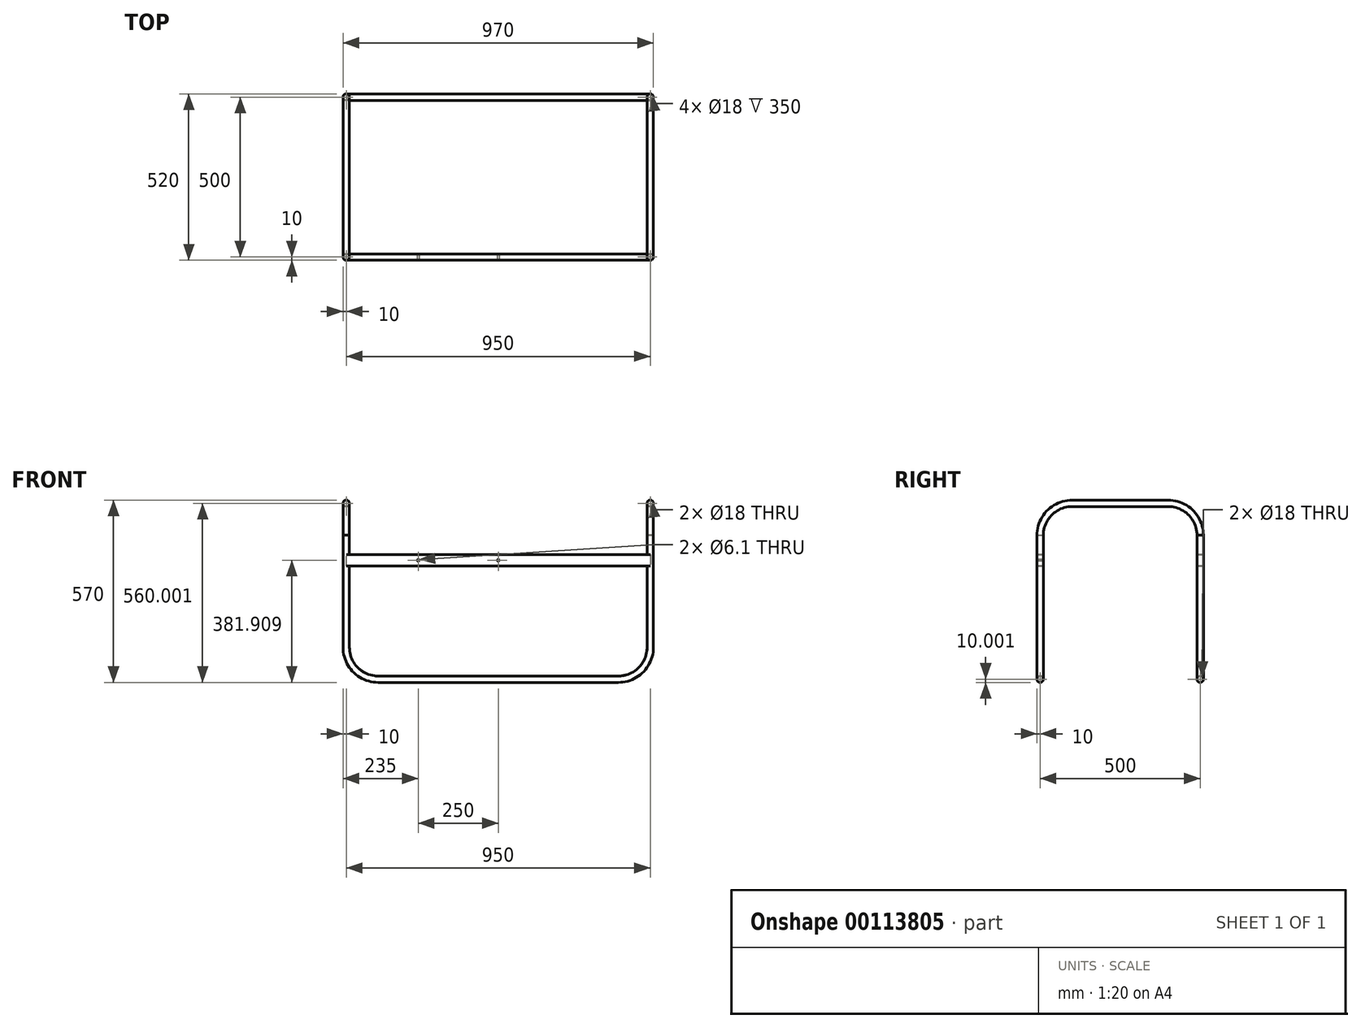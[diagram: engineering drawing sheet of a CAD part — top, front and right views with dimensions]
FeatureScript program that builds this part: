
annotation { "Feature Type Name" : "Feature", "Feature Type Description" : "" }
export const myFeature = defineFeature(function(context is Context, id is Id, definition is map)
    precondition{}
    {
        {
            var Q0;
            Q0=qCreatedBy(makeId("Front.planeOp"),FACE);
            var sketch = newSketch(context, id + "F0", { "sketchPlane" : qUnion([Q0])});
            skLineSegment(sketch, "E0.top", {"start": v(600, -233.58) * mm, "end": v(-150, -233.58) * mm});
            skPoint(sketch, "E1.visualSharp", {"position": v(-150, -233.58) * mm});
            skArc(sketch, "E1.filletArc", {"start": v(-250, -133.58) * mm, "mid": v(-220.71, -204.29) * mm, "end": v(-150, -233.58) * mm});
            skPoint(sketch, "E2.visualSharp", {"position": v(600, -233.58) * mm});
            skArc(sketch, "E2.filletArc", {"start": v(600, -233.58) * mm, "mid": v(670.71, -204.29) * mm, "end": v(700, -133.58) * mm});
            skLineSegment(sketch, "E3", {"start": v(-250, -133.58) * mm, "end": v(-250, 216.42) * mm});
            skLineSegment(sketch, "E4", {"start": v(700, -133.58) * mm, "end": v(700, 216.42) * mm});
            skLineSegment(sketch, "E5", {"start": v(-250, 156.03) * mm, "end": v(700, 156.03) * mm});
            skLineSegment(sketch, "E6", {"start": v(-250, 120.63) * mm, "end": v(700, 120.63) * mm});
            skSolve(sketch);
        }
        {
            var Q0;
            Q0=sQuery(id+"F0.wireOp",VERTEX,"E4.start");
            var Q1;
            Q1=sQuery(id+"F0.wireOp",EDGE,"E0.top");
            cPlane(context, id + "F1", {"entities" : qUnion([Q0, Q1]), "cplaneType" : CPlaneType.LINE_POINT, "offset" : 350 * mm, "width" : 150 * mm, "height" : 150 * mm});
        }
        {
            var Q0;
            Q0=qCreatedBy(id+"F1.planeOp",FACE);
            var sketch = newSketch(context, id + "F2", { "sketchPlane" : qUnion([Q0])});
            skPoint(sketch, "E7.0", {"position": v(0, -175) * mm});
            skLineSegment(sketch, "E8", {"start": v(-100, 316.42) * mm, "end": v(-194.41, 316.42) * mm});
            skPoint(sketch, "E9.0", {"position": v(-500, 216.42) * mm});
            skArc(sketch, "E10", {"start": v(-400, 316.42) * mm, "mid": v(-470.71, 287.13) * mm, "end": v(-500, 216.42) * mm});
            skPoint(sketch, "E11.0", {"position": v(0, 216.42) * mm});
            skArc(sketch, "E12", {"start": v(-100, 316.42) * mm, "mid": v(-77.01, 313.74) * mm, "end": v(-55.26, 305.85) * mm});
            skArc(sketch, "E13", {"start": v(-55.26, 305.85) * mm, "mid": v(-14.93, 268.98) * mm, "end": v(0, 216.42) * mm});
            skPoint(sketch, "E14", {"position": v(-194.77, 316.42) * mm});
            skLineSegment(sketch, "E15", {"start": v(-194.41, 316.42) * mm, "end": v(-400, 316.42) * mm});
            skSolve(sketch);
        }
        {
            var Q0;
            Q0=sQuery(id+"F2.wireOp",EDGE,"E10");
            var Q1;
            Q1=sQuery(id+"F2.wireOp",VERTEX,"E9.0");
            cPlane(context, id + "F3", {"entities" : qUnion([Q0, Q1]), "cplaneType" : CPlaneType.CURVE_POINT, "offset" : 700 * mm, "oppositeDirection" : true, "width" : 150 * mm, "height" : 150 * mm});
        }
        {
            var Q0;
            Q0=qCreatedBy(id+"F3.planeOp",FACE);
            var sketch = newSketch(context, id + "F4", { "sketchPlane" : qUnion([Q0])});
            skPoint(sketch, "E16.0", {"position": v(700, 0) * mm});
            skPoint(sketch, "E17.0", {"position": v(700, -500) * mm});
            skCircle(sketch, "E18", {"center": v(700, -500) * mm, "radius": 10 * mm});
            skCircle(sketch, "E19", {"center": v(700, -500) * mm, "radius": 9 * mm});
            skSolve(sketch);
        }
        {
            var Q0;
            Q0=makeQuery(id+"F4.imprint","IMPRINT",FACE,{"disambiguationData":[TD([[makeQuery(id+"F4.imprint","IMPRINT",EDGE,{"derivedFrom":sQuery(id+"F4.wireOp",EDGE,"E18")}),1.0]])]});
            var Q1;
            Q1=sQuery(id+"F2.wireOp",EDGE,"E10");
            var Q2;
            Q2=sQuery(id+"F2.wireOp",EDGE,"E15");
            var Q3;
            Q3=sQuery(id+"F2.wireOp",EDGE,"E8");
            var Q4;
            Q4=sQuery(id+"F2.wireOp",EDGE,"E12");
            var Q5;
            Q5=sQuery(id+"F2.wireOp",EDGE,"E13");
            var Q6;
            Q6=sQuery(id+"F0.wireOp",EDGE,"E4");
            var Q7;
            Q7=sQuery(id+"F0.wireOp",EDGE,"E2.filletArc");
            var Q8;
            Q8=sQuery(id+"F0.wireOp",EDGE,"E0.top");
            var Q9;
            Q9=sQuery(id+"F0.wireOp",EDGE,"E1.filletArc");
            var Q10;
            Q10=sQuery(id+"F0.wireOp",EDGE,"E3");
            sweep(context, id + "F5", {"profiles" : qUnion([Q0]), "path" : qUnion([Q1, Q2, Q3, Q4, Q5, Q6, Q7, Q8, Q9, Q10])});
        }
        {
            var Q0;
            {var subQ0=sQuery(id+"F0.wireOp",EDGE,"E5");Q0=makeQuery(id+"F0.imprint","IMPRINT",FACE,{"disambiguationData":[TD([[makeQuery(id+"F0.imprint","IMPRINT",EDGE,{"derivedFrom":subQ0}),-1.0]])]});}
            extrude(context, id + "F6", {"entities" : qUnion([Q0]), "operationType" : NewBodyOperationType.ADD, "endBound" : BoundingType.SYMMETRIC, "depth" : 20 * mm});
        }
        {
            var Q0;
            Q0=sQuery(id+"F2.wireOp",VERTEX,"E11.0");
            var Q1;
            Q1=sQuery(id+"F0.wireOp",VERTEX,"E3.end");
            var Q2;
            Q2=sQuery(id+"F4.wireOp",VERTEX,"E17.0");
            cPlane(context, id + "F7", {"entities" : qUnion([Q0, Q1, Q2]), "cplaneType" : CPlaneType.THREE_POINT, "offset" : 150 * mm, "width" : 150 * mm, "height" : 150 * mm});
        }
        {
            var Q0;
            Q0=qCreatedBy(id+"F7.planeOp",FACE);
            var sketch = newSketch(context, id + "F8", { "sketchPlane" : qUnion([Q0])});
            skPoint(sketch, "E20.0", {"position": v(-250, 0) * mm});
            skPoint(sketch, "E21.0", {"position": v(700, 500) * mm});
            skLineSegment(sketch, "E22", {"start": v(700, 500) * mm, "end": v(225, 250) * mm, "construction": true});
            skLineSegment(sketch, "E23", {"start": v(225, 250) * mm, "end": v(-250, 0) * mm, "construction": true});
            skSolve(sketch);
        }
        {
            var Q0;
            Q0=sQuery(id+"F8.wireOp",VERTEX,"E22.end");
            var Q1;
            Q1=makeQuery(id+"F0.imprint","IMPRINT",FACE,{"disambiguationData":[TD([[makeQuery(id+"F0.imprint","IMPRINT",EDGE,{"derivedFrom":sQuery(id+"F0.wireOp",EDGE,"E0.top")}),-1.0]])]});
            cPlane(context, id + "F9", {"entities" : qUnion([Q0, Q1]), "cplaneType" : CPlaneType.PLANE_POINT, "offset" : 150 * mm, "width" : 150 * mm, "height" : 150 * mm});
        }
        {
            var Q0;
            Q0=qCreatedBy(id+"F9.planeOp",FACE);
            var sketch = newSketch(context, id + "F10", { "sketchPlane" : qUnion([Q0])});
            skPoint(sketch, "E24.0", {"position": v(225, 216.42) * mm});
            skLineSegment(sketch, "E25", {"start": v(225, 216.42) * mm, "end": v(225, 152) * mm, "construction": true});
            skSolve(sketch);
        }
        {
            var Q0;
            Q0=makeQuery(id+"F5.opSweep","SWEPT_BODY",BODY,{"disambiguationData":[OSD([sQuery(id+"F0.wireOp",EDGE,"E3"),sQuery(id+"F4.wireOp",EDGE,"E18")])]});
            var Q1;
            Q1=sQuery(id+"F10.wireOp",EDGE,"E25");
            transform(context, id + "F11", {"entities" : qUnion([Q0]), "transformType" : TransformType.ROTATION, "transformAxis" : qUnion([Q1]), "angle" : 180 * degree, "makeCopy" : true});
        }
        {
            var Q0;
            Q0=makeQuery(id+"F6.opExtrude","CAP_FACE",FACE,{"disambiguationData":[OSD([sQuery(id+"F0.wireOp",EDGE,"E3"),sQuery(id+"F0.wireOp",EDGE,"E4"),sQuery(id+"F0.wireOp",EDGE,"E5"),sQuery(id+"F0.wireOp",EDGE,"E6")])],"isStart":false});
            var sketch = newSketch(context, id + "F12", { "sketchPlane" : qUnion([Q0])});
            skCircle(sketch, "E26", {"center": v(225, 138.33) * mm, "radius": 3.05 * mm});
            skPoint(sketch, "E26.centerSnap0", {"position": v(-250, 138.33) * mm});
            skPoint(sketch, "E26.centerSnap1", {"position": v(225, 156.03) * mm});
            skCircle(sketch, "E27", {"center": v(-25, 138.33) * mm, "radius": 3.05 * mm});
            skLineSegment(sketch, "E28.trimOffspring", {"start": v(-25, 138.33) * mm, "end": v(225, 138.33) * mm});
            skLineSegment(sketch, "E29", {"start": v(-250, 138.33) * mm, "end": v(-25, 138.33) * mm});
            skSolve(sketch);
        }
        {
            var Q0;
            Q0=sQuery(id+"F12.wireOp",VERTEX,"E28.trimOffspring.end");
            var Q1;
            Q1=sQuery(id+"F12.wireOp",VERTEX,"E27.center");
            var Q2;
            Q2=makeQuery(id+"F5.opSweep","SWEPT_BODY",BODY,{"disambiguationData":[OSD([sQuery(id+"F0.wireOp",EDGE,"E3"),sQuery(id+"F4.wireOp",EDGE,"E18")])]});
            hole(context, id + "F13", {"style" : HoleStyle.SIMPLE, "endStyle" : HoleEndStyle.THROUGH, "holeDiameter" : 6.1 * mm, "startFromSketch" : true, "locations" : qUnion([Q0, Q1]), "scope" : qUnion([Q2]), "isTappedThrough" : true});
        }
    });
